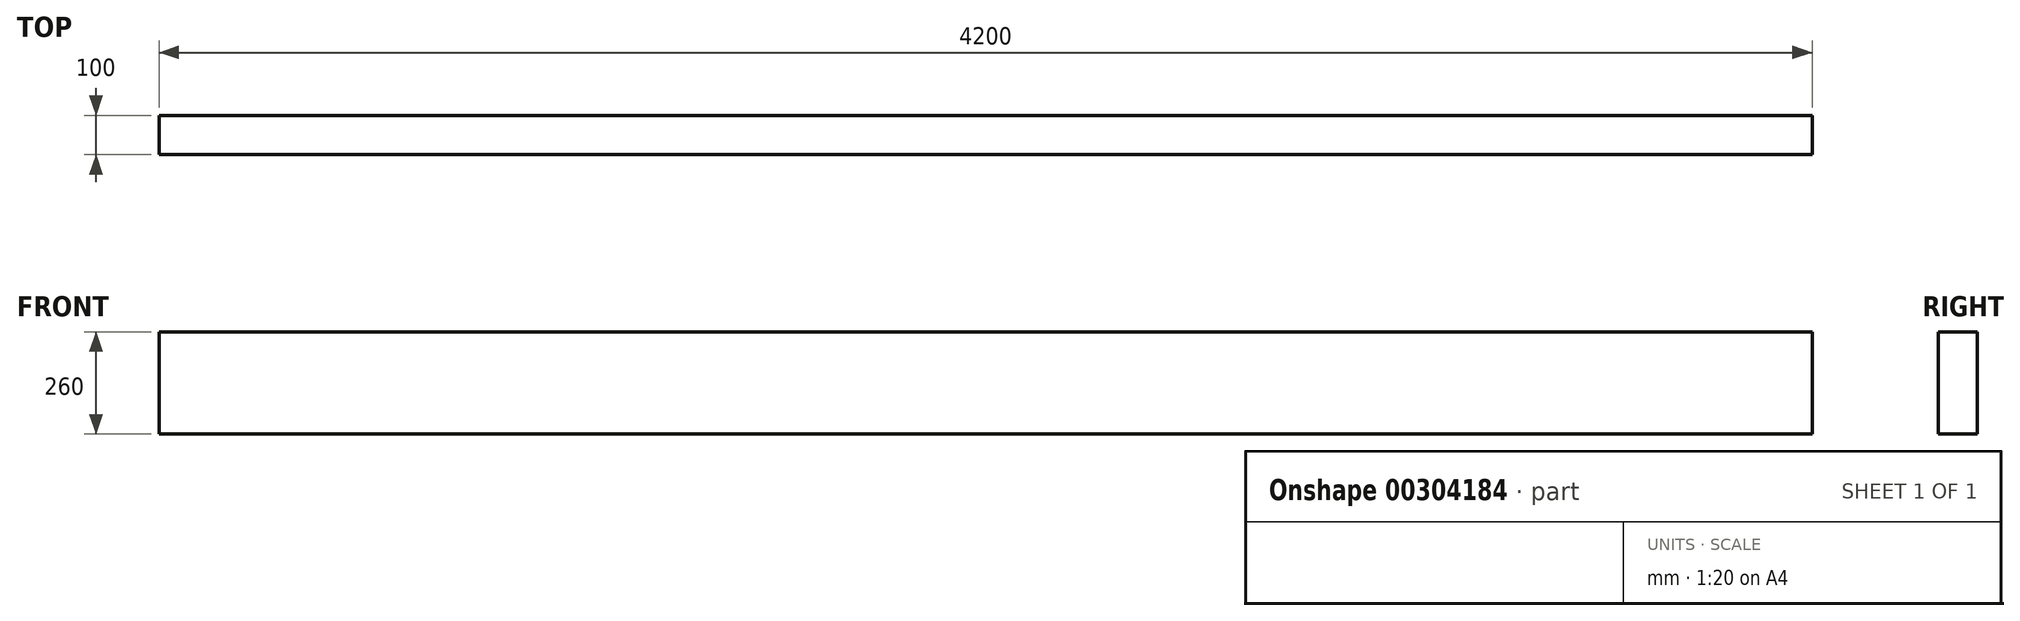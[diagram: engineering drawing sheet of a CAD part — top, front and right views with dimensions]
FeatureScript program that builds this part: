
annotation { "Feature Type Name" : "Feature", "Feature Type Description" : "" }
export const myFeature = defineFeature(function(context is Context, id is Id, definition is map)
    precondition{}
    {
        {
            var Q0;
            Q0=qCreatedBy(makeId("Top.planeOp"),FACE);
            var sketch = newSketch(context, id + "F0", { "sketchPlane" : qUnion([Q0])});
            skLineSegment(sketch, "E0.bottom", {"start": v(-2047.38, -21.46) * mm, "end": v(2152.62, -21.46) * mm});
            skLineSegment(sketch, "E0.top", {"start": v(-2047.38, -121.46) * mm, "end": v(2152.62, -121.46) * mm});
            skLineSegment(sketch, "E0.left", {"start": v(-2047.38, -21.46) * mm, "end": v(-2047.38, -121.46) * mm});
            skLineSegment(sketch, "E0.right", {"start": v(2152.62, -21.46) * mm, "end": v(2152.62, -121.46) * mm});
            skSolve(sketch);
        }
        {
            var Q0;
            Q0=makeQuery(id+"F0.imprint","IMPRINT",FACE,{"disambiguationData":[TD([[makeQuery(id+"F0.imprint","IMPRINT",EDGE,{"derivedFrom":sQuery(id+"F0.wireOp",EDGE,"E0.bottom")}),-1.0]])]});
            extrude(context, id + "F1", {"entities" : qUnion([Q0]), "offsetDistance" : 25 * mm, "depth" : 260 * mm});
        }
    });
